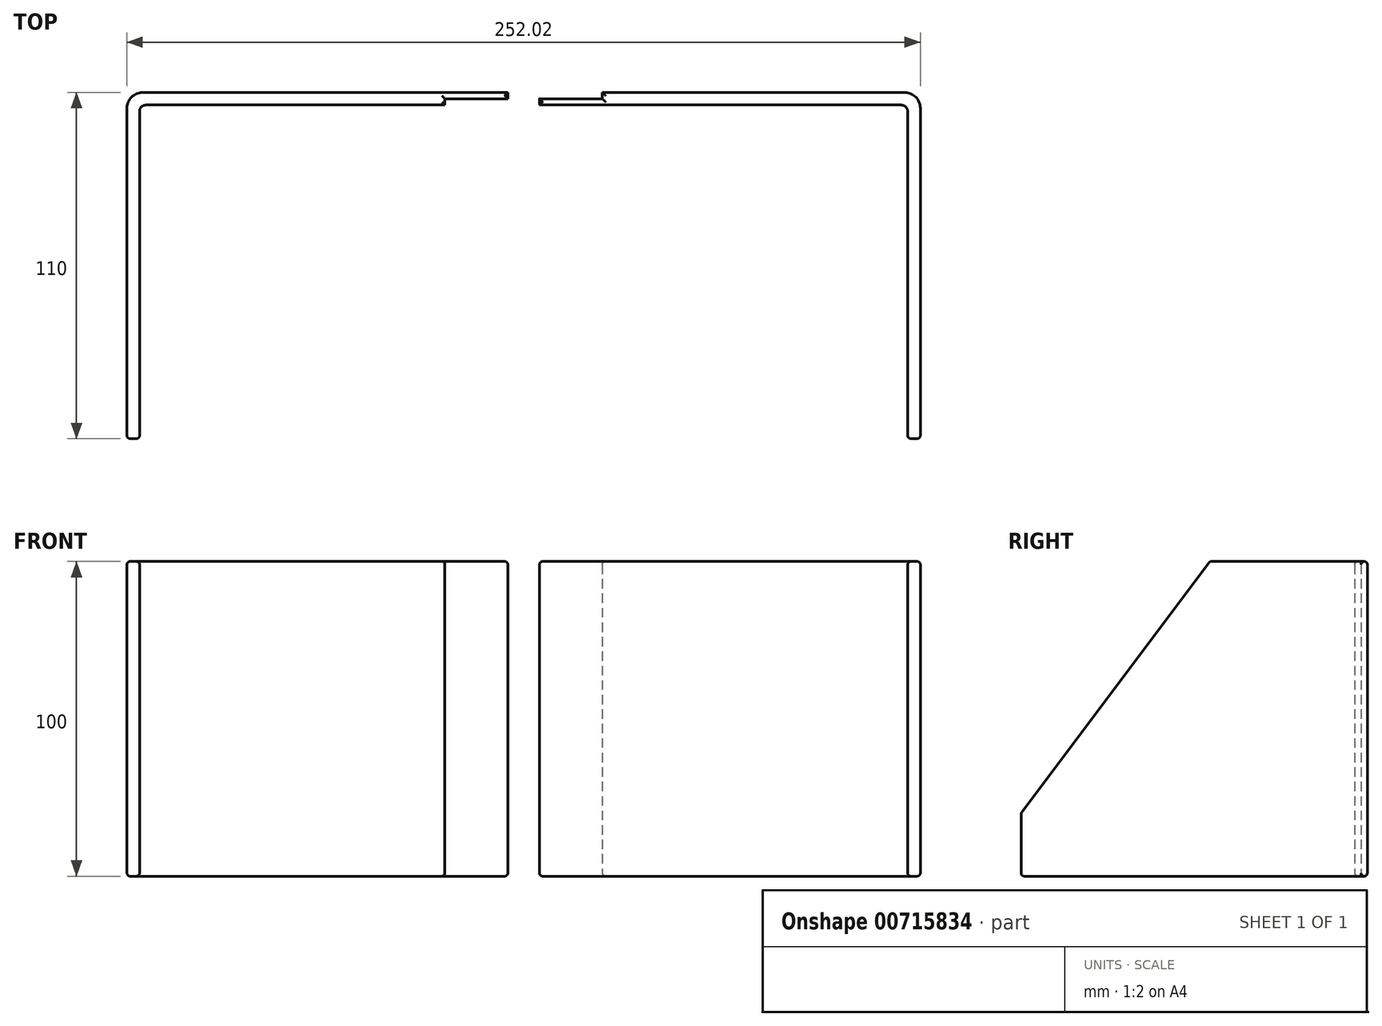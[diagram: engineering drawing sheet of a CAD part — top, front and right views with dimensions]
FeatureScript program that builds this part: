
annotation { "Feature Type Name" : "Feature", "Feature Type Description" : "" }
export const myFeature = defineFeature(function(context is Context, id is Id, definition is map)
    precondition{}
    {
        {
            var Q0;
            Q0=qCreatedBy(makeId("Top.planeOp"),FACE);
            var sketch = newSketch(context, id + "F0", { "sketchPlane" : qUnion([Q0])});
            skPoint(sketch, "E0", {"position": v(107, 0) * mm});
            skPoint(sketch, "E1", {"position": v(-10, 0) * mm});
            skPoint(sketch, "E2", {"position": v(10, 0) * mm});
            skPoint(sketch, "E3", {"position": v(107, -2) * mm});
            skPoint(sketch, "E4", {"position": v(107, -4) * mm});
            skPoint(sketch, "E5", {"position": v(-10, -4) * mm});
            skPoint(sketch, "E6", {"position": v(10, -2) * mm});
            skPoint(sketch, "E7", {"position": v(-10, -2) * mm});
            skLineSegment(sketch, "E8", {"start": v(10, 0) * mm, "end": v(10, -2) * mm});
            skLineSegment(sketch, "E9", {"start": v(10, -2) * mm, "end": v(-10, -2) * mm});
            skLineSegment(sketch, "E10", {"start": v(-10, -2) * mm, "end": v(-10, -4) * mm});
            skLineSegment(sketch, "E11", {"start": v(-10, -4) * mm, "end": v(107, -4) * mm});
            skLineSegment(sketch, "E12", {"start": v(10, 0) * mm, "end": v(107, 0) * mm});
            skPoint(sketch, "E13", {"position": v(111, 0) * mm});
            skLineSegment(sketch, "E14", {"start": v(107, -4) * mm, "end": v(107, -110) * mm});
            skLineSegment(sketch, "E15", {"start": v(107, -110) * mm, "end": v(111, -110) * mm});
            skLineSegment(sketch, "E16", {"start": v(111, -110) * mm, "end": v(111, 0) * mm});
            skLineSegment(sketch, "E17", {"start": v(111, 0) * mm, "end": v(107, 0) * mm});
            skPoint(sketch, "E18", {"position": v(-20.02, 0) * mm});
            skPoint(sketch, "E19", {"position": v(-40.02, 0) * mm});
            skPoint(sketch, "E20", {"position": v(-20.02, -2) * mm});
            skPoint(sketch, "E21", {"position": v(-20.02, -4) * mm});
            skPoint(sketch, "E22", {"position": v(-40.02, -4) * mm});
            skPoint(sketch, "E23", {"position": v(-40.02, -2) * mm});
            skLineSegment(sketch, "E24", {"start": v(-141.02, 0) * mm, "end": v(-20.02, 0) * mm});
            skLineSegment(sketch, "E25", {"start": v(-141.02, 0) * mm, "end": v(-141.02, -110) * mm});
            skLineSegment(sketch, "E26", {"start": v(-137.02, -4) * mm, "end": v(-40.02, -4) * mm});
            skLineSegment(sketch, "E27", {"start": v(-141.02, -110) * mm, "end": v(-137.02, -110) * mm});
            skLineSegment(sketch, "E28", {"start": v(-137.02, -110) * mm, "end": v(-137.02, -4) * mm});
            skLineSegment(sketch, "E29", {"start": v(-20.02, 0) * mm, "end": v(-20.02, -2) * mm});
            skLineSegment(sketch, "E30", {"start": v(-20.02, -2) * mm, "end": v(-40.02, -2) * mm});
            skLineSegment(sketch, "E31", {"start": v(-40.02, -2) * mm, "end": v(-40.02, -4) * mm});
            skSolve(sketch);
        }
        {
            var Q0;
            Q0=makeQuery(id+"F0.imprint","IMPRINT",FACE,{"disambiguationData":[TD([[makeQuery(id+"F0.imprint","IMPRINT",EDGE,{"derivedFrom":sQuery(id+"F0.wireOp",EDGE,"E8")}),1.0]])]});
            extrude(context, id + "F1", {"entities" : qUnion([Q0]), "depth" : 100 * mm, "offsetDistance" : 25 * mm});
        }
        {
            var Q0;
            Q0=makeQuery(id+"F0.imprint","IMPRINT",FACE,{"disambiguationData":[TD([[makeQuery(id+"F0.imprint","IMPRINT",EDGE,{"derivedFrom":sQuery(id+"F0.wireOp",EDGE,"E24")}),-1.0]])]});
            extrude(context, id + "F2", {"entities" : qUnion([Q0]), "depth" : 100 * mm, "offsetDistance" : 25 * mm});
        }
        {
            var Q0;
            Q0=makeQuery(id+"F1.opExtrude","SWEPT_FACE",FACE,{"disambiguationData":[OSD([sQuery(id+"F0.wireOp",EDGE,"E16")])]});
            var sketch = newSketch(context, id + "F3", { "sketchPlane" : qUnion([Q0])});
            skPoint(sketch, "E32", {"position": v(-110, 20) * mm});
            skPoint(sketch, "E33", {"position": v(-50, 100) * mm});
            skPoint(sketch, "E34", {"position": v(-110, 100) * mm});
            skLineSegment(sketch, "E35", {"start": v(-50, 100) * mm, "end": v(-110, 100) * mm});
            skLineSegment(sketch, "E36", {"start": v(-110, 100) * mm, "end": v(-110, 20) * mm});
            skLineSegment(sketch, "E37", {"start": v(-110, 20) * mm, "end": v(-50, 100) * mm});
            skSolve(sketch);
        }
        {
            var Q0;
            Q0=makeQuery(id+"F3.imprint","IMPRINT",FACE,{"disambiguationData":[TD([[makeQuery(id+"F3.imprint","IMPRINT",EDGE,{"derivedFrom":sQuery(id+"F3.wireOp",EDGE,"E35")}),-1.0]])]});
            extrude(context, id + "F4", {"entities" : qUnion([Q0]), "operationType" : NewBodyOperationType.REMOVE, "oppositeDirection" : true, "depth" : 25 * mm, "offsetDistance" : 25 * mm});
        }
        {
            var Q0;
            Q0=makeQuery(id+"F2.opExtrude","SWEPT_FACE",FACE,{"disambiguationData":[OSD([sQuery(id+"F0.wireOp",EDGE,"E25")])]});
            var sketch = newSketch(context, id + "F5", { "sketchPlane" : qUnion([Q0])});
            skPoint(sketch, "E38", {"position": v(50, 100) * mm});
            skPoint(sketch, "E39", {"position": v(110, 20) * mm});
            skPoint(sketch, "E40", {"position": v(110, 100) * mm});
            skLineSegment(sketch, "E41", {"start": v(50, 100) * mm, "end": v(110, 100) * mm});
            skLineSegment(sketch, "E42", {"start": v(110, 100) * mm, "end": v(110, 20) * mm});
            skLineSegment(sketch, "E43", {"start": v(110, 20) * mm, "end": v(50, 100) * mm});
            skSolve(sketch);
        }
        {
            var Q0;
            Q0=makeQuery(id+"F5.imprint","IMPRINT",FACE,{"disambiguationData":[TD([[makeQuery(id+"F5.imprint","IMPRINT",EDGE,{"derivedFrom":sQuery(id+"F5.wireOp",EDGE,"E41")}),-1.0]])]});
            extrude(context, id + "F6", {"entities" : qUnion([Q0]), "operationType" : NewBodyOperationType.REMOVE, "oppositeDirection" : true, "depth" : 25 * mm, "offsetDistance" : 25 * mm});
        }
        {
            var Q0;
            Q0=makeQuery(id+"F1.opExtrude","SWEPT_EDGE",EDGE,{"disambiguationData":[OSD([sQuery(id+"F0.wireOp",EDGE,"E16"),sQuery(id+"F0.wireOp",EDGE,"E17")])]});
            var Q1;
            Q1=makeQuery(id+"F2.opExtrude","SWEPT_EDGE",EDGE,{"disambiguationData":[OSD([sQuery(id+"F0.wireOp",EDGE,"E24"),sQuery(id+"F0.wireOp",EDGE,"E25")])]});
            fillet(context, id + "F7", {"entities" : qUnion([Q0, Q1]), "radius" : 5 * mm, "tangentPropagation" : true, "allowEdgeOverflow" : false});
        }
        {
            var Q0;
            Q0=makeQuery(id+"F2.opExtrude","SWEPT_EDGE",EDGE,{"disambiguationData":[OSD([sQuery(id+"F0.wireOp",EDGE,"E26"),sQuery(id+"F0.wireOp",EDGE,"E28")])]});
            var Q1;
            Q1=makeQuery(id+"F1.opExtrude","SWEPT_EDGE",EDGE,{"disambiguationData":[OSD([sQuery(id+"F0.wireOp",EDGE,"E11"),sQuery(id+"F0.wireOp",EDGE,"E14")])]});
            fillet(context, id + "F8", {"entities" : qUnion([Q0, Q1]), "radius" : 2 * mm, "tangentPropagation" : true, "allowEdgeOverflow" : false});
        }
        {
            var Q0;
            Q0=makeQuery(id+"F2.opExtrude","CAP_FACE",FACE,{"disambiguationData":[OSD([sQuery(id+"F0.wireOp",EDGE,"E24"),sQuery(id+"F0.wireOp",EDGE,"E25"),sQuery(id+"F0.wireOp",EDGE,"E26"),sQuery(id+"F0.wireOp",EDGE,"E27"),sQuery(id+"F0.wireOp",EDGE,"E28"),sQuery(id+"F0.wireOp",EDGE,"E29"),sQuery(id+"F0.wireOp",EDGE,"E30"),sQuery(id+"F0.wireOp",EDGE,"E31")])],"isStart":false});
            var Q1;
            Q1=makeQuery(id+"F6.boolean.opBoolean","COPY",FACE,{"derivedFrom":makeQuery(id+"F6.opExtrude","SWEPT_FACE",FACE,{"disambiguationData":[OSD([sQuery(id+"F5.wireOp",EDGE,"E43")])]})});
            var Q2;
            Q2=makeQuery(id+"F1.opExtrude","CAP_FACE",FACE,{"disambiguationData":[OSD([sQuery(id+"F0.wireOp",EDGE,"E8"),sQuery(id+"F0.wireOp",EDGE,"E9"),sQuery(id+"F0.wireOp",EDGE,"E10"),sQuery(id+"F0.wireOp",EDGE,"E11"),sQuery(id+"F0.wireOp",EDGE,"E12"),sQuery(id+"F0.wireOp",EDGE,"E14"),sQuery(id+"F0.wireOp",EDGE,"E15"),sQuery(id+"F0.wireOp",EDGE,"E16"),sQuery(id+"F0.wireOp",EDGE,"E17")])],"isStart":false});
            var Q3;
            Q3=makeQuery(id+"F4.boolean.opBoolean","COPY",FACE,{"derivedFrom":makeQuery(id+"F4.opExtrude","SWEPT_FACE",FACE,{"disambiguationData":[OSD([sQuery(id+"F3.wireOp",EDGE,"E37")])]})});
            var Q4;
            Q4=makeQuery(id+"F1.opExtrude","CAP_FACE",FACE,{"disambiguationData":[OSD([sQuery(id+"F0.wireOp",EDGE,"E8"),sQuery(id+"F0.wireOp",EDGE,"E9"),sQuery(id+"F0.wireOp",EDGE,"E10"),sQuery(id+"F0.wireOp",EDGE,"E11"),sQuery(id+"F0.wireOp",EDGE,"E12"),sQuery(id+"F0.wireOp",EDGE,"E14"),sQuery(id+"F0.wireOp",EDGE,"E15"),sQuery(id+"F0.wireOp",EDGE,"E16"),sQuery(id+"F0.wireOp",EDGE,"E17")])],"isStart":true});
            var Q5;
            Q5=makeQuery(id+"F2.opExtrude","CAP_FACE",FACE,{"disambiguationData":[OSD([sQuery(id+"F0.wireOp",EDGE,"E24"),sQuery(id+"F0.wireOp",EDGE,"E25"),sQuery(id+"F0.wireOp",EDGE,"E26"),sQuery(id+"F0.wireOp",EDGE,"E27"),sQuery(id+"F0.wireOp",EDGE,"E28"),sQuery(id+"F0.wireOp",EDGE,"E29"),sQuery(id+"F0.wireOp",EDGE,"E30"),sQuery(id+"F0.wireOp",EDGE,"E31")])],"isStart":true});
            var Q6;
            Q6=makeQuery(id+"F1.opExtrude","SWEPT_FACE",FACE,{"disambiguationData":[OSD([sQuery(id+"F0.wireOp",EDGE,"E15")])]});
            var Q7;
            Q7=makeQuery(id+"F2.opExtrude","SWEPT_FACE",FACE,{"disambiguationData":[OSD([sQuery(id+"F0.wireOp",EDGE,"E27")])]});
            fillet(context, id + "F9", {"entities" : qUnion([Q0, Q1, Q2, Q3, Q4, Q5, Q6, Q7]), "radius" : 1 * mm, "tangentPropagation" : true, "allowEdgeOverflow" : false});
        }
    });
